# Revit family: FP-Revit19-DH9060H1-Dryer-90002785A
name_source: partatom
category: Specialty Equipment
units: mm (PartAtom-declared; Revit-internal decimal feet)

## family parameters
Always vertical = Yes
Cut with Voids When Loaded = Yes
Part Type = Normal
Room Calculation Point = No
Round Connector Dimension = Use Diameter
Shared = No
Work Plane-Based = No

## types (2) — shared parameters
Cavity - Depth = 665 mm  [stored 2.18176 ft]
Cavity - Height (857mm - 867mm) = 862 mm  [stored 2.82808 ft]
Cavity - Width = 624 mm  [stored 2.04724 ft]
Chassis - Depth = 576 mm
Chassis - Height = 827 mm  [stored 2.71325 ft]
Chassis - Width = 600 mm  [stored 1.9685 ft]
Connector Description - Electrical = 220 – 240 V, 50 Hz, 10 A circuit
Connector Description - Sanitary = Drain to tub or standpipe, MAX 1000mm - MIN 600mm high
Connector Description - Water = Water connection supplied from washer
Description = Heat Pump Dryer
Manufacturer = Fisher & Paykel Appliances Ltd
Material - Body = Fisher & Paykel - Grey
Material - Display Panel = Fisher & Paykel - Glass, Black
Material - Glass = Fisher & Paykel - Glass, Black
Material - Trim = Fisher & Paykel - Steel, Chrome Plated
Product - Depth = 654 mm
Product - Height (845mm - 855mm) = 850 mm  [stored 2.78871 ft]
Product - Width = 600 mm  [stored 1.9685 ft]
Visibility - Clearance Required = Yes
zero-valued in all types: Default Elevation

## per-type parameters (varying)
| type | Material - Buttons and Dials | Material - Door | Material - Front |
| DH9060HG1 | Fisher & Paykel - Stainless Steel (Dark) | Fisher & Paykel - Grey, Charcoal | Fisher & Paykel - Grey, Charcoal |
| DH9060H1 | Fisher & Paykel - Stainless Steel | Fisher & Paykel - Steel, Chrome Plated | Fisher & Paykel - White |

note: column(s) folded — value = type name in every type: Model

note: [stored X ft] marks values corroborated as IEEE doubles in the binary element streams (Revit-internal decimal feet)

## geometry (parser evidence)
native form markers: Sweep x1
no freeform markers — native parametric forms only
